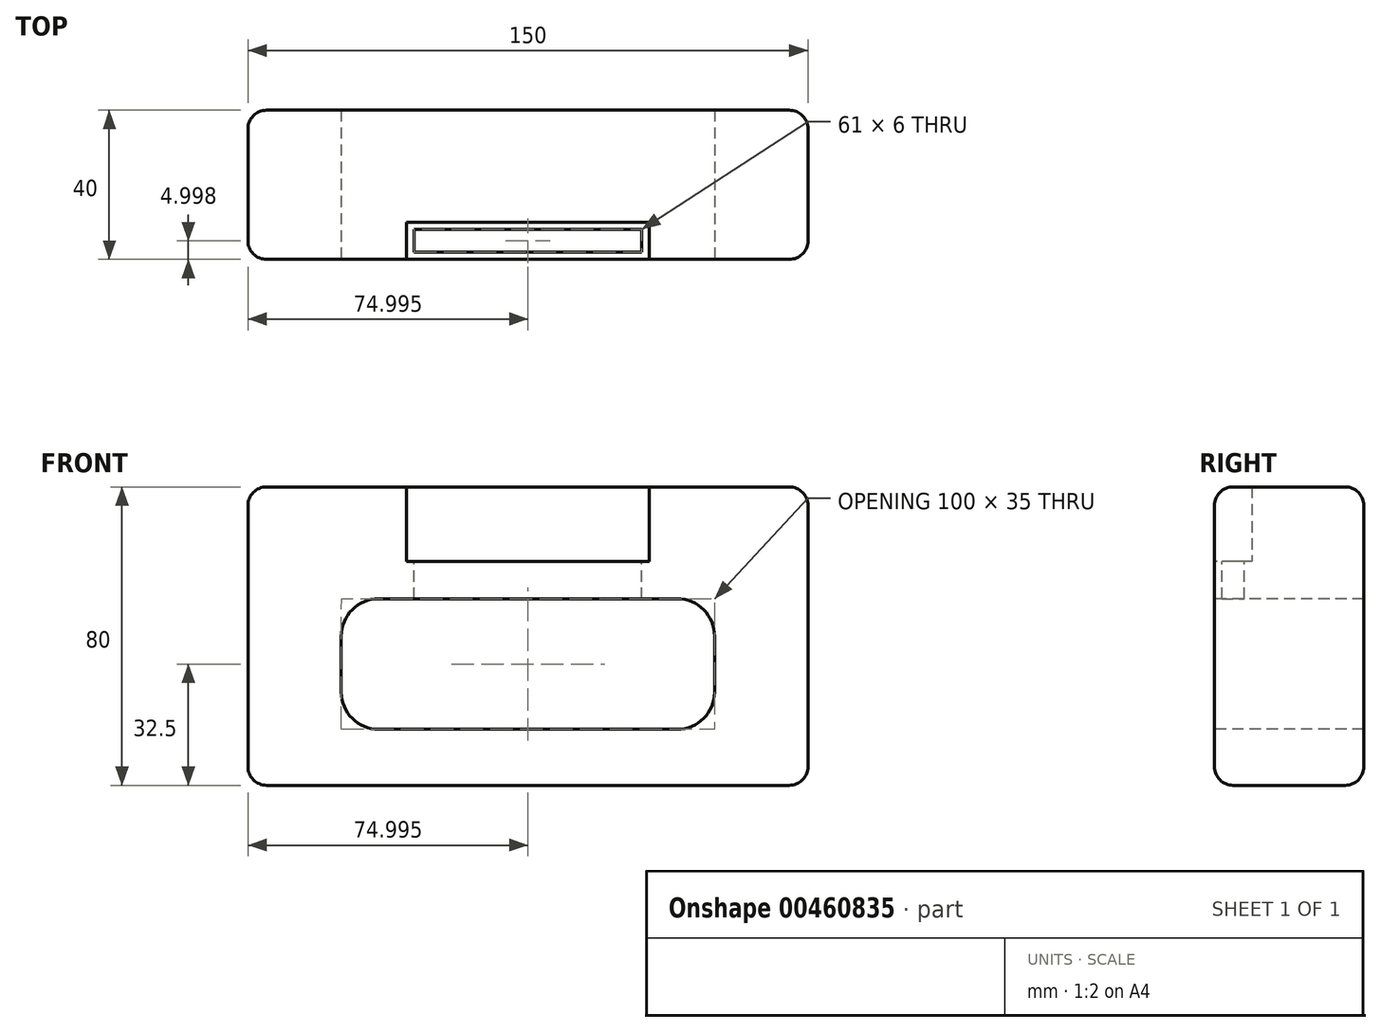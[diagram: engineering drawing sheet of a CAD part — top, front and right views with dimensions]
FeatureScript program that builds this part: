
annotation { "Feature Type Name" : "Feature", "Feature Type Description" : "" }
export const myFeature = defineFeature(function(context is Context, id is Id, definition is map)
    precondition{}
    {
        {
            var Q0;
            Q0=qCreatedBy(makeId("Top.planeOp"),FACE);
            var sketch = newSketch(context, id + "F0", { "sketchPlane" : qUnion([Q0])});
            skLineSegment(sketch, "E0.bottom", {"start": v(-89.1, 18.86) * mm, "end": v(60.9, 18.86) * mm});
            skLineSegment(sketch, "E0.top", {"start": v(-89.1, -21.14) * mm, "end": v(60.9, -21.14) * mm});
            skLineSegment(sketch, "E0.left", {"start": v(-89.1, 18.86) * mm, "end": v(-89.1, -21.14) * mm});
            skLineSegment(sketch, "E0.right", {"start": v(60.9, 18.86) * mm, "end": v(60.9, -21.14) * mm});
            skSolve(sketch);
        }
        {
            var Q0;
            Q0=makeQuery(id+"F0.imprint","IMPRINT",FACE,{"disambiguationData":[TD([[makeQuery(id+"F0.imprint","IMPRINT",EDGE,{"derivedFrom":sQuery(id+"F0.wireOp",EDGE,"E0.bottom")}),-1.0]])]});
            extrude(context, id + "F1", {"entities" : qUnion([Q0]), "depth" : 80 * mm});
        }
        {
            var Q0;
            Q0=makeQuery(id+"F1.opExtrude","SWEPT_FACE",FACE,{"disambiguationData":[OSD([sQuery(id+"F0.wireOp",EDGE,"E0.top")])]});
            var sketch = newSketch(context, id + "F2", { "sketchPlane" : qUnion([Q0])});
            skLineSegment(sketch, "E1.bottom", {"start": v(-46.6, 80) * mm, "end": v(18.4, 80) * mm});
            skLineSegment(sketch, "E1.top", {"start": v(-46.6, 60) * mm, "end": v(18.4, 60) * mm});
            skLineSegment(sketch, "E1.left", {"start": v(-46.6, 80) * mm, "end": v(-46.6, 60) * mm});
            skLineSegment(sketch, "E1.right", {"start": v(18.4, 80) * mm, "end": v(18.4, 60) * mm});
            skSolve(sketch);
        }
        {
            var Q0;
            Q0 = qSketchRegion(id + "F2", true);
            extrude(context, id + "F3", {"entities" : qUnion([Q0]), "operationType" : NewBodyOperationType.REMOVE, "oppositeDirection" : true, "depth" : 10 * mm});
        }
        {
            var Q0;
            Q0=makeQuery(id+"F1.opExtrude","SWEPT_FACE",FACE,{"disambiguationData":[OSD([sQuery(id+"F0.wireOp",EDGE,"E0.top")])]});
            var sketch = newSketch(context, id + "F4", { "sketchPlane" : qUnion([Q0])});
            skLineSegment(sketch, "E2.bottom", {"start": v(-54.1, 50) * mm, "end": v(25.9, 50) * mm});
            skLineSegment(sketch, "E2.top", {"start": v(-54.1, 15) * mm, "end": v(25.9, 15) * mm});
            skLineSegment(sketch, "E2.left", {"start": v(-64.1, 40) * mm, "end": v(-64.1, 25) * mm});
            skLineSegment(sketch, "E2.right", {"start": v(35.9, 40) * mm, "end": v(35.9, 25) * mm});
            skPoint(sketch, "E3.visualSharp", {"position": v(-64.1, 50) * mm});
            skArc(sketch, "E3.filletArc", {"start": v(-54.1, 50) * mm, "mid": v(-61.17, 47.07) * mm, "end": v(-64.1, 40) * mm});
            skPoint(sketch, "E4.visualSharp", {"position": v(-64.1, 15) * mm});
            skArc(sketch, "E4.filletArc", {"start": v(-64.1, 25) * mm, "mid": v(-61.17, 17.93) * mm, "end": v(-54.1, 15) * mm});
            skPoint(sketch, "E5.visualSharp", {"position": v(35.9, 50) * mm});
            skArc(sketch, "E5.filletArc", {"start": v(35.9, 40) * mm, "mid": v(32.98, 47.07) * mm, "end": v(25.9, 50) * mm});
            skPoint(sketch, "E6.visualSharp", {"position": v(35.9, 15) * mm});
            skArc(sketch, "E6.filletArc", {"start": v(25.9, 15) * mm, "mid": v(32.98, 17.93) * mm, "end": v(35.9, 25) * mm});
            skSolve(sketch);
        }
        {
            var Q0;
            Q0=makeQuery(id+"F4.imprint","IMPRINT",FACE,{"disambiguationData":[TD([[makeQuery(id+"F4.imprint","IMPRINT",EDGE,{"derivedFrom":sQuery(id+"F4.wireOp",EDGE,"E2.bottom")}),-1.0]])]});
            extrude(context, id + "F5", {"entities" : qUnion([Q0]), "operationType" : NewBodyOperationType.REMOVE, "oppositeDirection" : true, "depth" : 287 * mm});
        }
        {
            var Q0;
            Q0=makeQuery(id+"F3.boolean.opBoolean","COPY",FACE,{"derivedFrom":makeQuery(id+"F3.opExtrude","SWEPT_FACE",FACE,{"disambiguationData":[OSD([sQuery(id+"F2.wireOp",EDGE,"E1.top")])]})});
            var sketch = newSketch(context, id + "F6", { "sketchPlane" : qUnion([Q0])});
            skLineSegment(sketch, "E7.bottom", {"start": v(-44.6, -13.14) * mm, "end": v(16.4, -13.14) * mm});
            skLineSegment(sketch, "E7.top", {"start": v(-44.6, -19.14) * mm, "end": v(16.4, -19.14) * mm});
            skLineSegment(sketch, "E7.left", {"start": v(-44.6, -13.14) * mm, "end": v(-44.6, -19.14) * mm});
            skLineSegment(sketch, "E7.right", {"start": v(16.4, -13.14) * mm, "end": v(16.4, -19.14) * mm});
            skSolve(sketch);
        }
        {
            var Q0;
            Q0=makeQuery(id+"F6.imprint","IMPRINT",FACE,{"disambiguationData":[TD([[makeQuery(id+"F6.imprint","IMPRINT",EDGE,{"derivedFrom":sQuery(id+"F6.wireOp",EDGE,"E7.bottom")}),-1.0]])]});
            extrude(context, id + "F7", {"entities" : qUnion([Q0]), "operationType" : NewBodyOperationType.REMOVE, "oppositeDirection" : true, "depth" : 25 * mm});
        }
        {
            var Q0;
            Q0=makeQuery(id+"F3.boolean.opBoolean","COPY",EDGE,{"derivedFrom":makeQuery(id+"F3.opExtrude","CAP_EDGE",EDGE,{"disambiguationData":[OSD([sQuery(id+"F2.wireOp",EDGE,"E1.bottom")])],"isStart":false})});
            var Q1;
            Q1=makeQuery(id+"F1.opExtrude","SWEPT_EDGE",EDGE,{"disambiguationData":[OSD([sQuery(id+"F0.wireOp",EDGE,"E0.top"),sQuery(id+"F0.wireOp",EDGE,"E0.left")])]});
            var Q2;
            Q2=makeQuery(id+"F1.opExtrude","SWEPT_EDGE",EDGE,{"disambiguationData":[OSD([sQuery(id+"F0.wireOp",EDGE,"E0.top"),sQuery(id+"F0.wireOp",EDGE,"E0.right")])]});
            var Q3;
            {var subQ0=sQuery(id+"F0.wireOp",EDGE,"E0.right");var subQ1=sQuery(id+"F0.wireOp",EDGE,"E0.top");Q3=makeQuery(id+"F3.boolean.opBoolean","SPLIT",EDGE,{"disambiguationData":[TD([makeQuery(id+"F1.opExtrude","SWEPT_FACE",FACE,{"disambiguationData":[OSD([subQ0])]})])],"derivedFrom":makeQuery(id+"F1.opExtrude","CAP_EDGE",EDGE,{"disambiguationData":[OSD([subQ1])],"isStart":false})});}
            var Q4;
            {var subQ0=sQuery(id+"F0.wireOp",EDGE,"E0.left");var subQ1=sQuery(id+"F0.wireOp",EDGE,"E0.top");Q4=makeQuery(id+"F3.boolean.opBoolean","SPLIT",EDGE,{"disambiguationData":[TD([makeQuery(id+"F1.opExtrude","SWEPT_FACE",FACE,{"disambiguationData":[OSD([subQ0])]})])],"derivedFrom":makeQuery(id+"F1.opExtrude","CAP_EDGE",EDGE,{"disambiguationData":[OSD([subQ1])],"isStart":false})});}
            var Q5;
            Q5=makeQuery(id+"F1.opExtrude","CAP_FACE",FACE,{"disambiguationData":[OSD([sQuery(id+"F0.wireOp",EDGE,"E0.bottom"),sQuery(id+"F0.wireOp",EDGE,"E0.top"),sQuery(id+"F0.wireOp",EDGE,"E0.left"),sQuery(id+"F0.wireOp",EDGE,"E0.right")])],"isStart":true});
            var Q6;
            Q6=makeQuery(id+"F1.opExtrude","SWEPT_EDGE",EDGE,{"disambiguationData":[OSD([sQuery(id+"F0.wireOp",EDGE,"E0.bottom"),sQuery(id+"F0.wireOp",EDGE,"E0.left")])]});
            var Q7;
            Q7=makeQuery(id+"F1.opExtrude","CAP_EDGE",EDGE,{"disambiguationData":[OSD([sQuery(id+"F0.wireOp",EDGE,"E0.left")])],"isStart":false});
            var Q8;
            Q8=makeQuery(id+"F1.opExtrude","CAP_EDGE",EDGE,{"disambiguationData":[OSD([sQuery(id+"F0.wireOp",EDGE,"E0.bottom")])],"isStart":false});
            var Q9;
            Q9=makeQuery(id+"F1.opExtrude","CAP_EDGE",EDGE,{"disambiguationData":[OSD([sQuery(id+"F0.wireOp",EDGE,"E0.right")])],"isStart":false});
            var Q10;
            Q10=makeQuery(id+"F1.opExtrude","SWEPT_EDGE",EDGE,{"disambiguationData":[OSD([sQuery(id+"F0.wireOp",EDGE,"E0.bottom"),sQuery(id+"F0.wireOp",EDGE,"E0.right")])]});
            var Q11;
            Q11=makeQuery(id+"F3.boolean.opBoolean","COPY",EDGE,{"derivedFrom":makeQuery(id+"F3.opExtrude","CAP_EDGE",EDGE,{"disambiguationData":[OSD([sQuery(id+"F2.wireOp",EDGE,"E1.top")])],"isStart":true})});
            var Q12;
            Q12=makeQuery(id+"F3.boolean.opBoolean","COPY",EDGE,{"derivedFrom":makeQuery(id+"F3.opExtrude","CAP_EDGE",EDGE,{"disambiguationData":[OSD([sQuery(id+"F2.wireOp",EDGE,"E1.left")])],"isStart":true})});
            var Q13;
            Q13=makeQuery(id+"F3.boolean.opBoolean","COPY",EDGE,{"derivedFrom":makeQuery(id+"F3.opExtrude","CAP_EDGE",EDGE,{"disambiguationData":[OSD([sQuery(id+"F2.wireOp",EDGE,"E1.right")])],"isStart":true})});
            var Q14;
            Q14=makeQuery(id+"F3.boolean.opBoolean","COPY",EDGE,{"derivedFrom":makeQuery(id+"F3.opExtrude","SWEPT_EDGE",EDGE,{"disambiguationData":[OSD([sQuery(id+"F0.wireOp",EDGE,"E0.top"),sQuery(id+"F2.wireOp",EDGE,"E1.bottom"),sQuery(id+"F2.wireOp",EDGE,"E1.left")])]})});
            var Q15;
            Q15=makeQuery(id+"F3.boolean.opBoolean","COPY",EDGE,{"derivedFrom":makeQuery(id+"F3.opExtrude","SWEPT_EDGE",EDGE,{"disambiguationData":[OSD([sQuery(id+"F0.wireOp",EDGE,"E0.top"),sQuery(id+"F2.wireOp",EDGE,"E1.bottom"),sQuery(id+"F2.wireOp",EDGE,"E1.right")])]})});
            fillet(context, id + "F8", {"entities" : qUnion([Q0, Q1, Q2, Q3, Q4, Q5, Q6, Q7, Q8, Q9, Q10, Q11, Q12, Q13, Q14, Q15]), "radius" : 5 * mm, "tangentPropagation" : true, "allowEdgeOverflow" : false});
        }
    });
